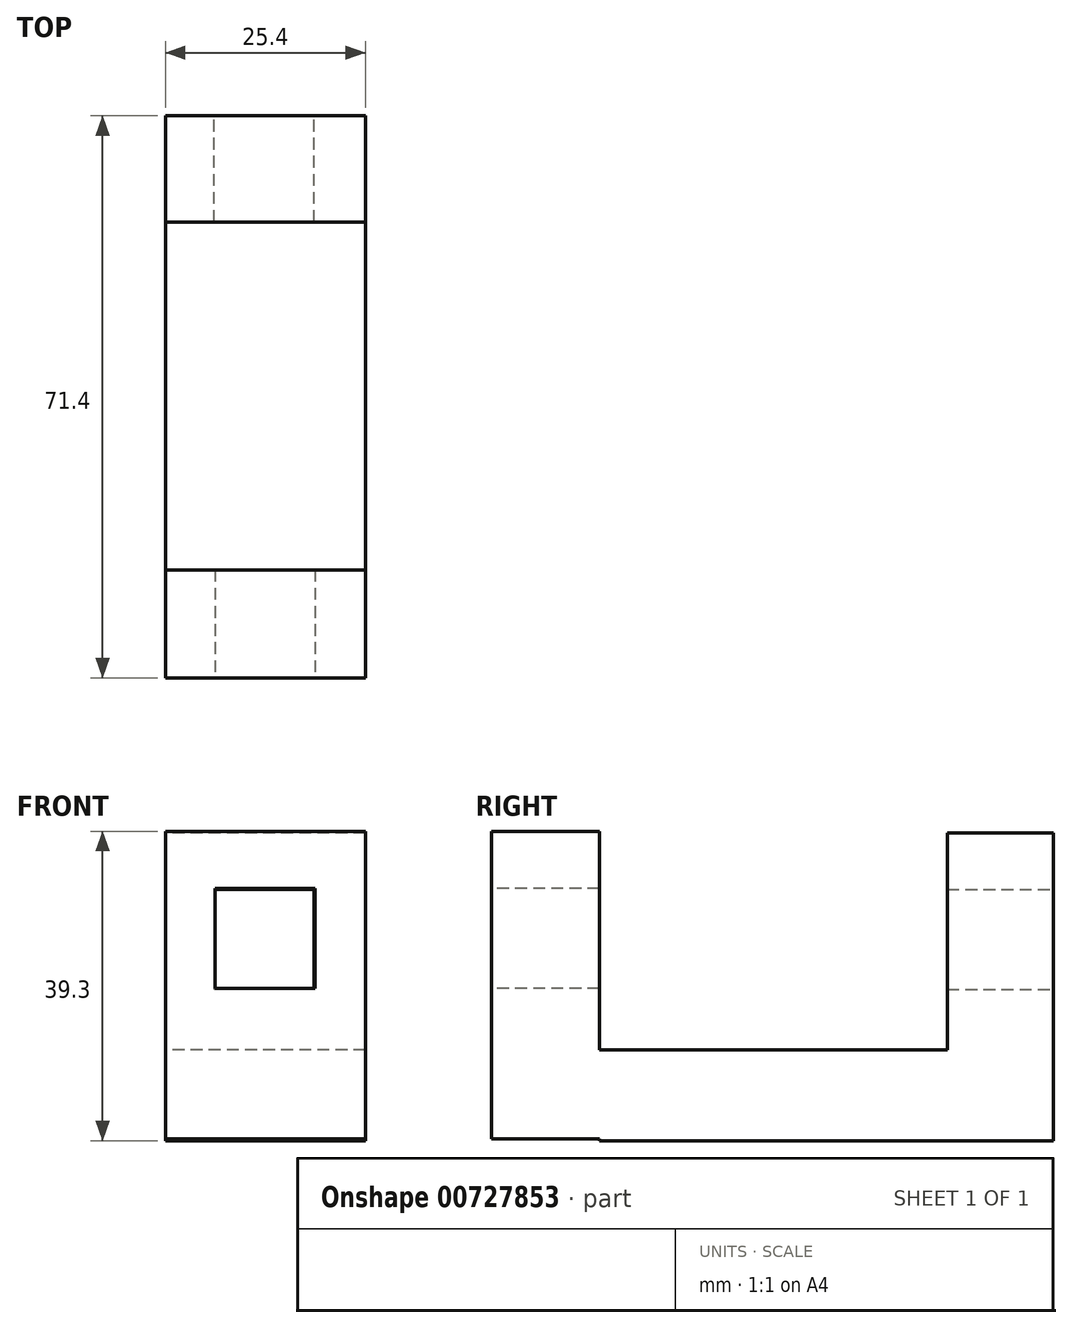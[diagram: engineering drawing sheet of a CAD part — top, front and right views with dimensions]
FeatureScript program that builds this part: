
annotation { "Feature Type Name" : "Feature", "Feature Type Description" : "" }
export const myFeature = defineFeature(function(context is Context, id is Id, definition is map)
    precondition{}
    {
        {
            var Q0;
            Q0=qCreatedBy(makeId("Right.planeOp"),FACE);
            var sketch = newSketch(context, id + "F0", { "sketchPlane" : qUnion([Q0])});
            skLineSegment(sketch, "E0.bottom", {"start": v(-34.77, 27.8) * mm, "end": v(-21.05, 27.8) * mm});
            skLineSegment(sketch, "E0.top", {"start": v(-34.77, -11.28) * mm, "end": v(-21.05, -11.28) * mm});
            skLineSegment(sketch, "E0.left", {"start": v(-34.77, 27.8) * mm, "end": v(-34.77, -11.28) * mm});
            skLineSegment(sketch, "E1.bottom", {"start": v(-21.05, 0) * mm, "end": v(23.14, 0) * mm});
            skLineSegment(sketch, "E1.top", {"start": v(-21.05, -11.51) * mm, "end": v(23.14, -11.51) * mm});
            skLineSegment(sketch, "E1.left", {"start": v(-21.05, -11.28) * mm, "end": v(-21.05, -11.51) * mm});
            skLineSegment(sketch, "E2.bottom", {"start": v(23.14, -11.51) * mm, "end": v(36.63, -11.51) * mm});
            skLineSegment(sketch, "E2.top", {"start": v(23.14, 27.56) * mm, "end": v(36.63, 27.56) * mm});
            skLineSegment(sketch, "E2.left", {"start": v(23.14, 0) * mm, "end": v(23.14, 27.56) * mm});
            skLineSegment(sketch, "E2.right", {"start": v(36.63, -11.51) * mm, "end": v(36.63, 27.56) * mm});
            skLineSegment(sketch, "E3", {"start": v(-21.05, 27.8) * mm, "end": v(-21.05, 0) * mm});
            skSolve(sketch);
        }
        {
            var Q0;
            Q0=makeQuery(id+"F0.imprint","IMPRINT",FACE,{"disambiguationData":[TD([[makeQuery(id+"F0.imprint","IMPRINT",EDGE,{"derivedFrom":sQuery(id+"F0.wireOp",EDGE,"E0.bottom")}),-1.0]])]});
            extrude(context, id + "F1", {"entities" : qUnion([Q0]), "depth" : 25.4 * mm, "offsetDistance" : 25.4 * mm});
        }
        {
            var Q0;
            Q0=makeQuery(id+"F0.imprint","IMPRINT",FACE,{"disambiguationData":[TD([[makeQuery(id+"F0.imprint","IMPRINT",EDGE,{"derivedFrom":sQuery(id+"F0.wireOp",EDGE,"E0.bottom")}),-1.0]])]});
            extrude(context, id + "F2", {"entities" : qUnion([Q0]), "operationType" : NewBodyOperationType.ADD, "depth" : 25.4 * mm, "offsetDistance" : 25.4 * mm});
        }
        {
            var Q0;
            Q0=makeQuery(id+"F1.opExtrude","SWEPT_FACE",FACE,{"disambiguationData":[OSD([sQuery(id+"F0.wireOp",EDGE,"E0.left")])]});
            var sketch = newSketch(context, id + "F3", { "sketchPlane" : qUnion([Q0])});
            skLineSegment(sketch, "E4.bottom", {"start": v(6.3, 20.55) * mm, "end": v(19, 20.55) * mm});
            skLineSegment(sketch, "E4.top", {"start": v(6.3, 7.85) * mm, "end": v(19, 7.85) * mm});
            skLineSegment(sketch, "E4.left", {"start": v(6.3, 20.55) * mm, "end": v(6.3, 7.85) * mm});
            skLineSegment(sketch, "E4.right", {"start": v(19, 20.55) * mm, "end": v(19, 7.85) * mm});
            skSolve(sketch);
        }
        {
            var Q0;
            Q0=makeQuery(id+"F3.imprint","IMPRINT",FACE,{"disambiguationData":[TD([[makeQuery(id+"F3.imprint","IMPRINT",EDGE,{"derivedFrom":sQuery(id+"F3.wireOp",EDGE,"E4.bottom")}),-1.0]])]});
            extrude(context, id + "F4", {"entities" : qUnion([Q0]), "operationType" : NewBodyOperationType.REMOVE, "oppositeDirection" : true, "depth" : 50.8 * mm, "offsetDistance" : 25.4 * mm});
        }
        {
            var Q0;
            Q0=makeQuery(id+"F1.opExtrude","SWEPT_FACE",FACE,{"disambiguationData":[OSD([sQuery(id+"F0.wireOp",EDGE,"E2.right")])]});
            var sketch = newSketch(context, id + "F5", { "sketchPlane" : qUnion([Q0])});
            skLineSegment(sketch, "E5.bottom", {"start": v(-18.86, 20.41) * mm, "end": v(-6.16, 20.41) * mm});
            skLineSegment(sketch, "E5.top", {"start": v(-18.86, 7.71) * mm, "end": v(-6.16, 7.71) * mm});
            skLineSegment(sketch, "E5.left", {"start": v(-18.86, 20.41) * mm, "end": v(-18.86, 7.71) * mm});
            skLineSegment(sketch, "E5.right", {"start": v(-6.16, 20.41) * mm, "end": v(-6.16, 7.71) * mm});
            skSolve(sketch);
        }
        {
            var Q0;
            Q0 = qSketchRegion(id + "F5", true);
            extrude(context, id + "F6", {"entities" : qUnion([Q0]), "operationType" : NewBodyOperationType.REMOVE, "oppositeDirection" : true, "depth" : 50.8 * mm, "offsetDistance" : 25.4 * mm});
        }
    });
